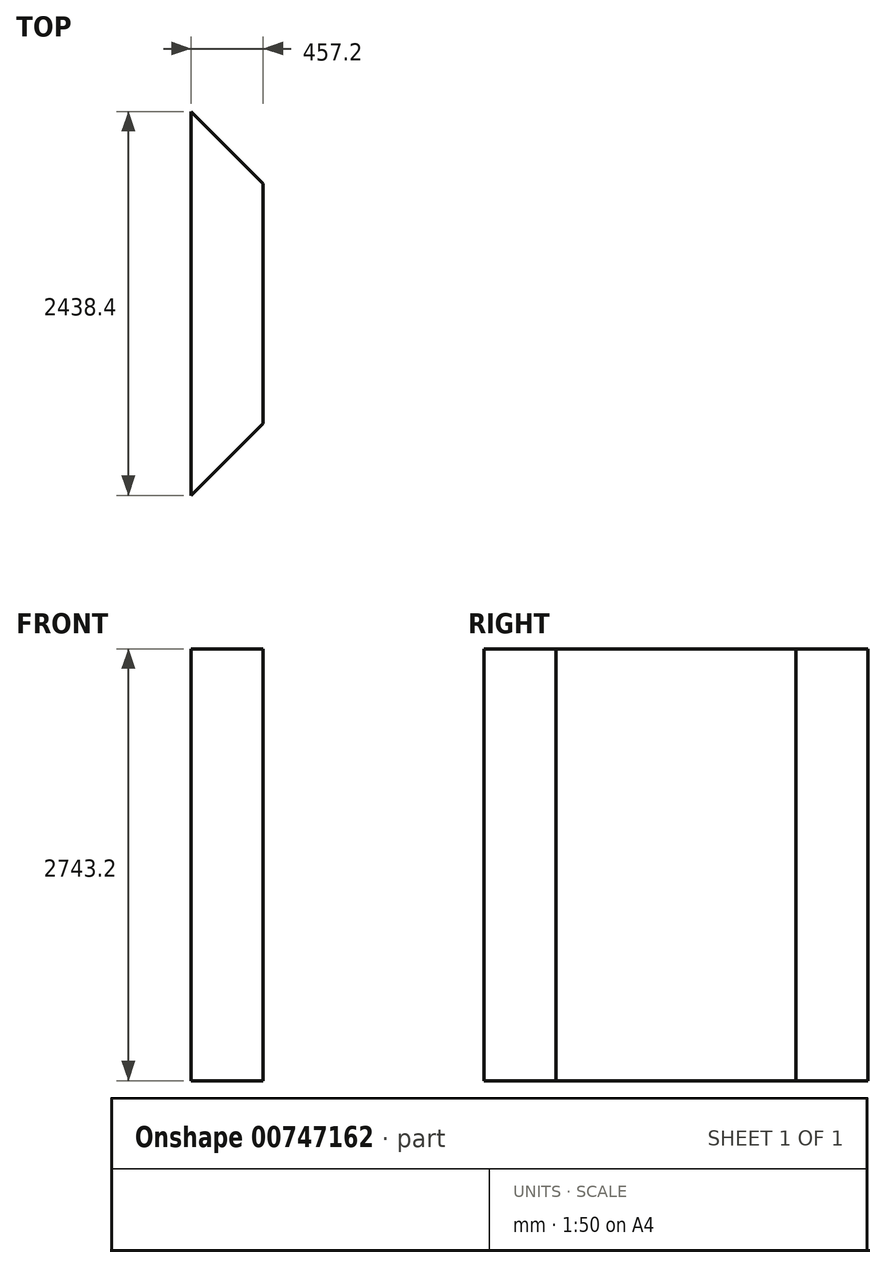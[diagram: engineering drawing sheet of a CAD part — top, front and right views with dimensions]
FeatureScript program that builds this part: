
annotation { "Feature Type Name" : "Feature", "Feature Type Description" : "" }
export const myFeature = defineFeature(function(context is Context, id is Id, definition is map)
    precondition{}
    {
        {
            var Q0;
            Q0=qCreatedBy(makeId("Top.planeOp"),FACE);
            var sketch = newSketch(context, id + "F0", { "sketchPlane" : qUnion([Q0])});
            skLineSegment(sketch, "E0.bottom", {"start": v(-354.5, 1301.31) * mm, "end": v(102.7, 1301.31) * mm});
            skLineSegment(sketch, "E0.top", {"start": v(-354.5, -1441.89) * mm, "end": v(102.7, -1441.89) * mm});
            skLineSegment(sketch, "E0.left", {"start": v(-354.5, 1301.31) * mm, "end": v(-354.5, -1441.89) * mm});
            skLineSegment(sketch, "E0.right", {"start": v(102.7, 1301.31) * mm, "end": v(102.7, -1441.89) * mm});
            skSolve(sketch);
        }
        {
            var Q0;
            Q0 = qSketchRegion(id + "F0", true);
            extrude(context, id + "F1", {"entities" : qUnion([Q0]), "depth" : 2743.2 * mm, "offsetDistance" : 25.4 * mm});
        }
        {
            var Q0;
            Q0=makeQuery(id+"F1.opExtrude","SWEPT_EDGE",EDGE,{"disambiguationData":[OSD([sQuery(id+"F0.wireOp",EDGE,"E0.top"),sQuery(id+"F0.wireOp",EDGE,"E0.right")])]});
            var Q1;
            Q1=makeQuery(id+"F1.opExtrude","SWEPT_EDGE",EDGE,{"disambiguationData":[OSD([sQuery(id+"F0.wireOp",EDGE,"E0.bottom"),sQuery(id+"F0.wireOp",EDGE,"E0.right")])]});
            chamfer(context, id + "F2", {"entities" : qUnion([Q0, Q1]), "width" : 609.6 * mm, "tangentPropagation" : true});
        }
    });
